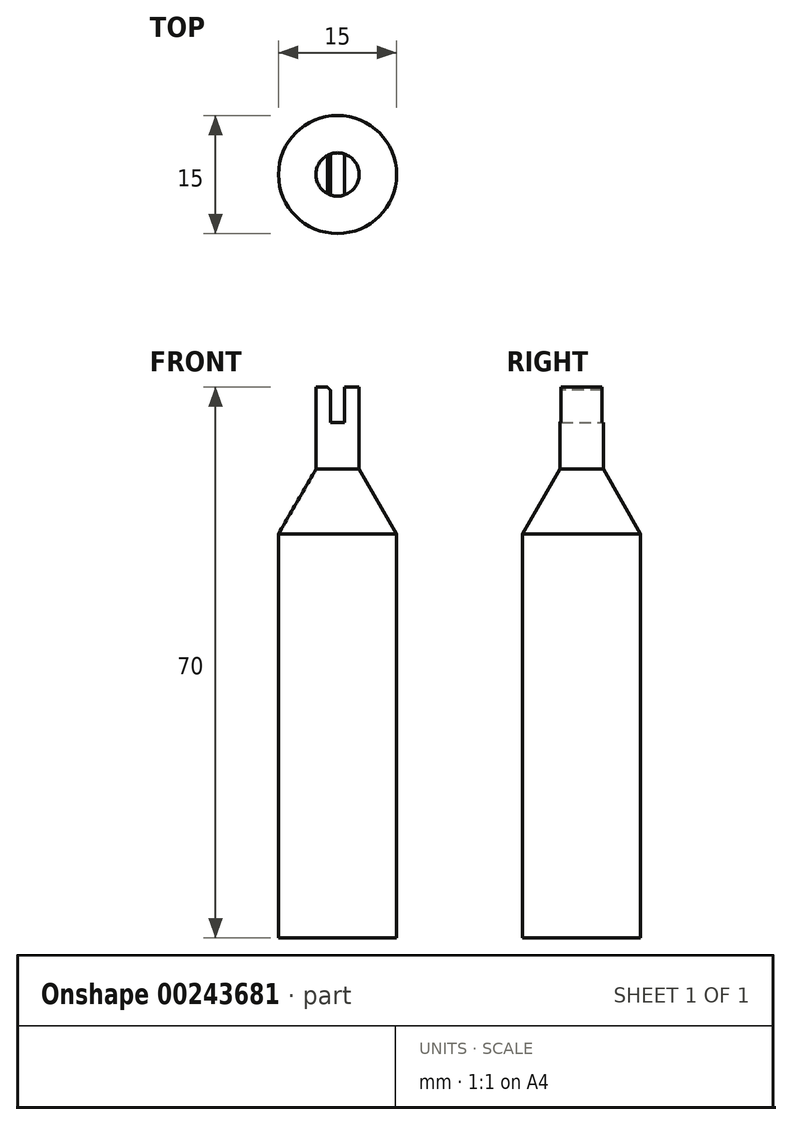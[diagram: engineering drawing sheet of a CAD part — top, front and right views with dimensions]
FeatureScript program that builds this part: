
annotation { "Feature Type Name" : "Feature", "Feature Type Description" : "" }
export const myFeature = defineFeature(function(context is Context, id is Id, definition is map)
    precondition{}
    {
        {
            var Q0;
            Q0=qCreatedBy(makeId("Top.planeOp"),FACE);
            var sketch = newSketch(context, id + "F0", { "sketchPlane" : qUnion([Q0])});
            skCircle(sketch, "E0", {"center": v(0, 0) * mm, "radius": 2.75 * mm});
            skCircle(sketch, "E1", {"center": v(0, 0) * mm, "radius": 7.5 * mm});
            skSolve(sketch);
        }
        {
            var Q0;
            Q0=makeQuery(id+"F0.imprint","IMPRINT",FACE,{"disambiguationData":[TD([[makeQuery(id+"F0.imprint","IMPRINT",EDGE,{"derivedFrom":sQuery(id+"F0.wireOp",EDGE,"E0")}),-1.0]])]});
            var Q1;
            Q1=makeQuery(id+"F0.imprint","IMPRINT",FACE,{"disambiguationData":[TD([[makeQuery(id+"F0.imprint","IMPRINT",EDGE,{"derivedFrom":sQuery(id+"F0.wireOp",EDGE,"E0")}),1.0]])]});
            extrude(context, id + "F1", {"entities" : qUnion([Q0, Q1]), "oppositeDirection" : true, "depth" : 60 * mm});
        }
        {
            var Q0;
            Q0=makeQuery(id+"F0.imprint","IMPRINT",FACE,{"disambiguationData":[TD([[makeQuery(id+"F0.imprint","IMPRINT",EDGE,{"derivedFrom":sQuery(id+"F0.wireOp",EDGE,"E0")}),1.0]])]});
            extrude(context, id + "F2", {"entities" : qUnion([Q0]), "operationType" : NewBodyOperationType.ADD, "depth" : 10 * mm});
        }
        {
            var Q0;
            Q0=makeQuery(id+"F1.opExtrude","CAP_EDGE",EDGE,{"disambiguationData":[OSD([sQuery(id+"F0.wireOp",EDGE,"E1")])],"isStart":true});
            chamfer(context, id + "F3", {"entities" : qUnion([Q0]), "chamferType" : ChamferType.OFFSET_ANGLE, "width" : 5 * mm, "oppositeDirection" : false, "angle" : 60 * degree, "tangentPropagation" : true});
        }
        {
            var Q0;
            Q0=makeQuery(id+"F2.opExtrude","CAP_FACE",FACE,{"disambiguationData":[OSD([sQuery(id+"F0.wireOp",EDGE,"E0")])],"isStart":false});
            var sketch = newSketch(context, id + "F4", { "sketchPlane" : qUnion([Q0])});
            skLineSegment(sketch, "E2.bottom", {"start": v(0.9, -4.53) * mm, "end": v(-0.9, -4.53) * mm});
            skLineSegment(sketch, "E2.top", {"start": v(0.9, 4.53) * mm, "end": v(-0.9, 4.53) * mm});
            skLineSegment(sketch, "E2.left", {"start": v(0.9, -4.53) * mm, "end": v(0.9, 4.53) * mm});
            skLineSegment(sketch, "E2.right", {"start": v(-0.9, -4.53) * mm, "end": v(-0.9, 4.53) * mm});
            skPoint(sketch, "E2.middle", {"position": v(0, 0) * mm});
            skSolve(sketch);
        }
        {
            var Q0;
            {var subQ0=sQuery(id+"F4.wireOp",EDGE,"E2.left");var subQ1=makeQuery(id+"F2.opExtrude","CAP_EDGE",EDGE,{"disambiguationData":[OSD([sQuery(id+"F0.wireOp",EDGE,"E0")])],"isStart":false});var subQ2=makeQuery(id+"F4.imprint","INTERSECT",VERTEX,{"disambiguationData":[OD(0.0)],"derivedFrom":[subQ1,subQ0]});Q0=makeQuery(id+"F4.imprint","IMPRINT",FACE,{"disambiguationData":[TD([[makeQuery(id+"F4.imprint","IMPRINT",EDGE,{"disambiguationData":[TD([[subQ2,-1.0]])],"derivedFrom":subQ0}),1.0]])]});}
            extrude(context, id + "F5", {"entities" : qUnion([Q0]), "operationType" : NewBodyOperationType.REMOVE, "oppositeDirection" : true, "depth" : 4.5 * mm});
        }
        {
            var Q0;
            Q0=makeQuery(id+"F5.boolean.opBoolean","COPY",EDGE,{"derivedFrom":makeQuery(id+"F5.opExtrude","CAP_EDGE",EDGE,{"disambiguationData":[OSD([sQuery(id+"F4.wireOp",EDGE,"E2.right")])],"isStart":true})});
            var Q1;
            Q1=makeQuery(id+"F5.boolean.opBoolean","COPY",EDGE,{"derivedFrom":makeQuery(id+"F5.opExtrude","CAP_EDGE",EDGE,{"disambiguationData":[OSD([sQuery(id+"F4.wireOp",EDGE,"E2.left")])],"isStart":true})});
            chamfer(context, id + "F6", {"entities" : qUnion([Q0, Q1]), "width" : .4 * mm, "tangentPropagation" : true});
        }
    });
